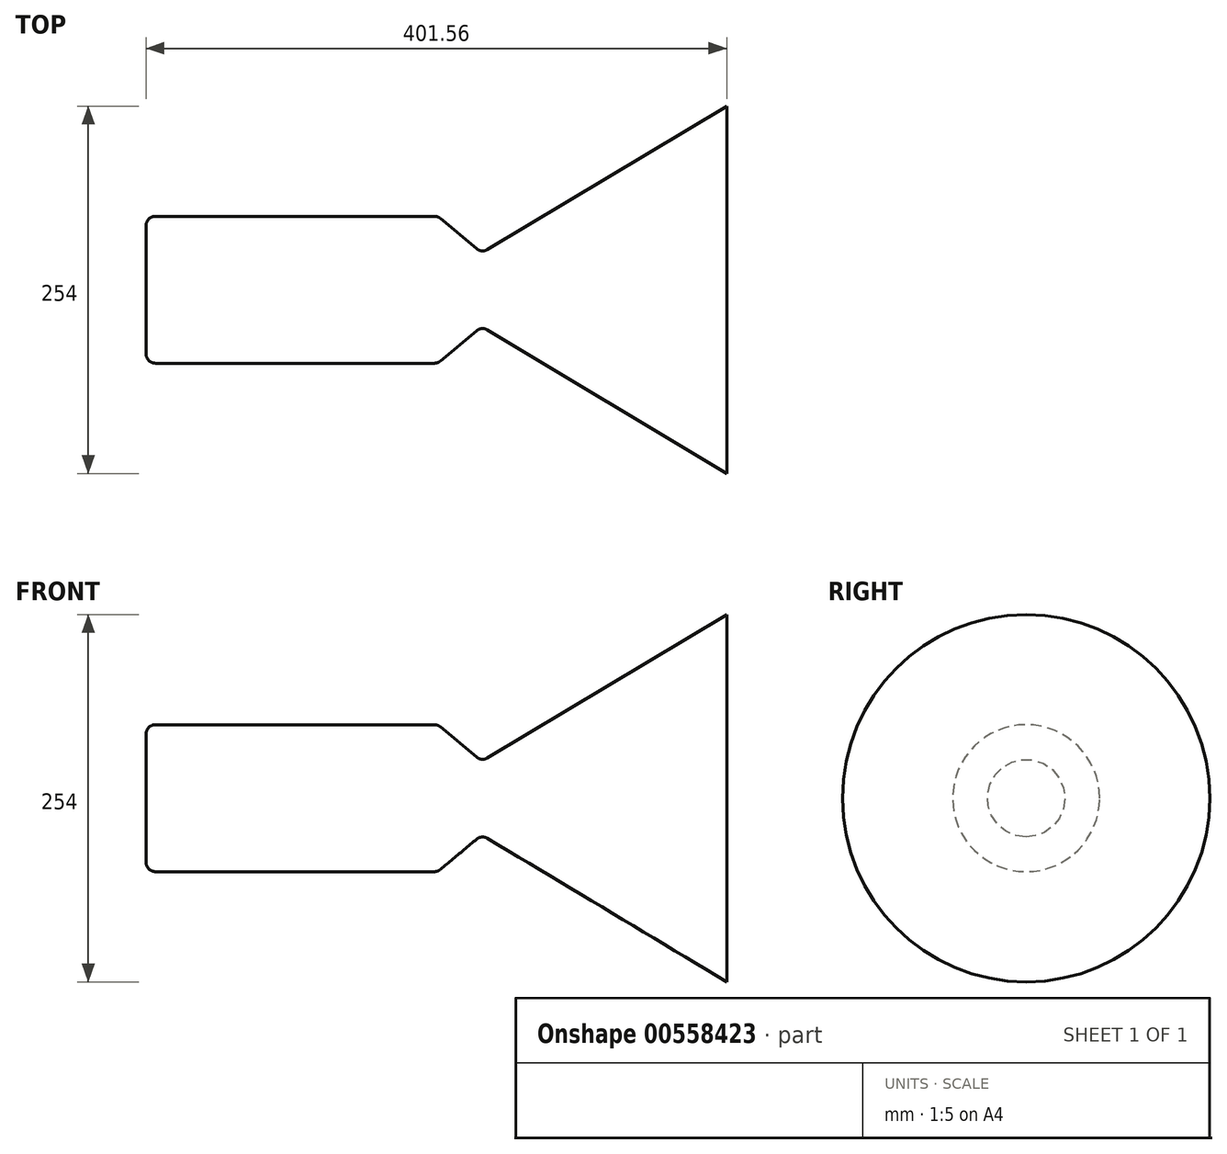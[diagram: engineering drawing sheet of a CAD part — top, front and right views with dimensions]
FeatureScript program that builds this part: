
annotation { "Feature Type Name" : "Feature", "Feature Type Description" : "" }
export const myFeature = defineFeature(function(context is Context, id is Id, definition is map)
    precondition{}
    {
        {
            var Q0;
            Q0=qCreatedBy(makeId("Front.planeOp"),FACE);
            var sketch = newSketch(context, id + "F0", { "sketchPlane" : qUnion([Q0])});
            skLineSegment(sketch, "E0", {"start": v(0, 0) * mm, "end": v(0, 44.45) * mm});
            skLineSegment(sketch, "E1", {"start": v(6.35, 50.8) * mm, "end": v(199.35, 50.8) * mm});
            skLineSegment(sketch, "E2", {"start": v(203.42, 49.32) * mm, "end": v(228.59, 28.3) * mm});
            skLineSegment(sketch, "E3", {"start": v(235.92, 27.72) * mm, "end": v(401.56, 127) * mm});
            skLineSegment(sketch, "E4", {"start": v(401.56, 127) * mm, "end": v(401.56, 0) * mm});
            skLineSegment(sketch, "E5", {"start": v(401.56, 0) * mm, "end": v(0, 0) * mm});
            skPoint(sketch, "E6.visualSharp", {"position": v(232.05, 25.4) * mm});
            skArc(sketch, "E6.filletArc", {"start": v(228.59, 28.3) * mm, "mid": v(232.16, 26.84) * mm, "end": v(235.92, 27.72) * mm});
            skPoint(sketch, "E7.visualSharp", {"position": v(201.65, 50.8) * mm});
            skArc(sketch, "E7.filletArc", {"start": v(203.42, 49.32) * mm, "mid": v(201.51, 50.42) * mm, "end": v(199.35, 50.8) * mm});
            skPoint(sketch, "E8.visualSharp", {"position": v(0, 50.8) * mm});
            skArc(sketch, "E8.filletArc", {"start": v(6.35, 50.8) * mm, "mid": v(1.86, 48.94) * mm, "end": v(0, 44.45) * mm});
            skSolve(sketch);
        }
        {
            var Q0;
            Q0 = qSketchRegion(id + "F0", true);
            var Q1;
            Q1=sQuery(id+"F0.wireOp",EDGE,"E5");
            revolve(context, id + "F1", {"entities" : qUnion([Q0]), "axis" : qUnion([Q1]), "revolveType" : RevolveType.FULL});
        }
    });
